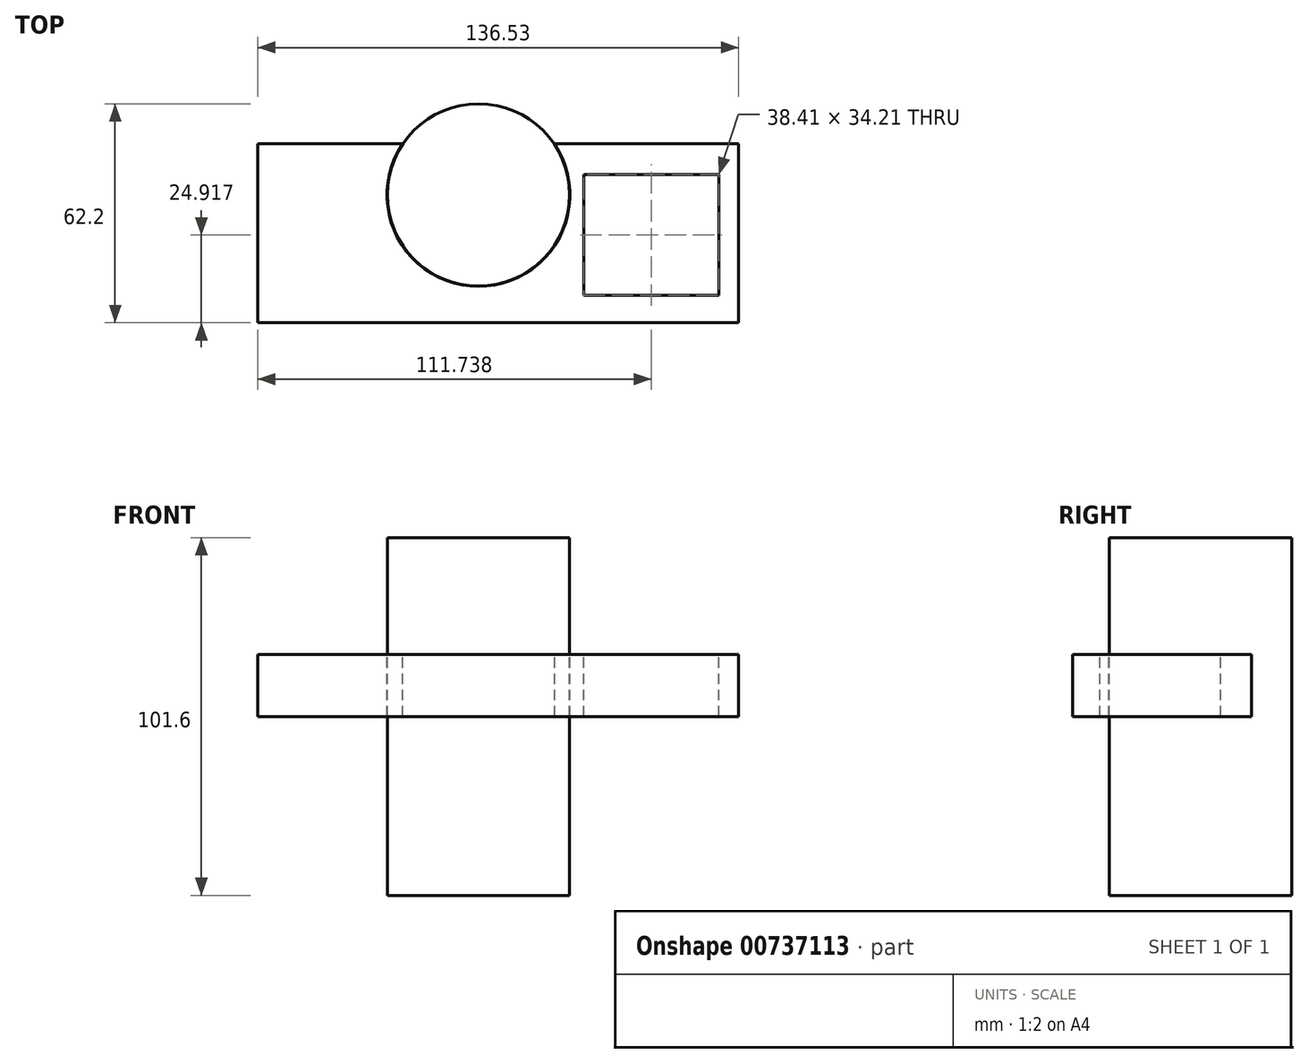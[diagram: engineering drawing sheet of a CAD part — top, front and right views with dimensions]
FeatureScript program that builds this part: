
annotation { "Feature Type Name" : "Feature", "Feature Type Description" : "" }
export const myFeature = defineFeature(function(context is Context, id is Id, definition is map)
    precondition{}
    {
        {
            var Q0;
            Q0=qCreatedBy(makeId("Front.planeOp"),FACE);
            var sketch = newSketch(context, id + "F0", { "sketchPlane" : qUnion([Q0])});
            skLineSegment(sketch, "E0.bottom", {"start": v(-42.1, 0) * mm, "end": v(94.42, 0) * mm});
            skLineSegment(sketch, "E0.top", {"start": v(-42.1, -17.58) * mm, "end": v(94.42, -17.58) * mm});
            skLineSegment(sketch, "E0.left", {"start": v(-42.1, 0) * mm, "end": v(-42.1, -17.58) * mm});
            skLineSegment(sketch, "E0.right", {"start": v(94.42, 0) * mm, "end": v(94.42, -17.58) * mm});
            skSolve(sketch);
        }
        {
            var Q0;
            Q0=makeQuery(id+"F0.imprint","IMPRINT",FACE,{"disambiguationData":[TD([[makeQuery(id+"F0.imprint","IMPRINT",EDGE,{"derivedFrom":sQuery(id+"F0.wireOp",EDGE,"E0.bottom")}),-1.0]])]});
            extrude(context, id + "F1", {"entities" : qUnion([Q0]), "depth" : 25.4 * mm, "offsetDistance" : 25.4 * mm, "hasSecondDirection" : true, "secondDirectionOppositeDirection" : true, "secondDirectionDepth" : 25.4 * mm});
        }
        {
            var Q0;
            Q0=makeQuery(id+"F1.opExtrude","SWEPT_FACE",FACE,{"disambiguationData":[OSD([sQuery(id+"F0.wireOp",EDGE,"E0.bottom")])]});
            var sketch = newSketch(context, id + "F2", { "sketchPlane" : qUnion([Q0])});
            skCircle(sketch, "E1", {"center": v(20.56, 10.92) * mm, "radius": 26 * mm});
            skSolve(sketch);
        }
        {
            var Q0;
            {var subQ0=sQuery(id+"F2.wireOp",EDGE,"E1");var subQ1=makeQuery(id+"F1.opExtrude","CAP_EDGE",EDGE,{"disambiguationData":[OSD([sQuery(id+"F0.wireOp",EDGE,"E0.bottom")])],"isStart":true});var subQ2=makeQuery(id+"F2.imprint","INTERSECT",VERTEX,{"disambiguationData":[OD(0.0)],"derivedFrom":[subQ1,subQ0]});Q0=makeQuery(id+"F2.imprint","IMPRINT",FACE,{"disambiguationData":[TD([[makeQuery(id+"F2.imprint","IMPRINT",EDGE,{"disambiguationData":[TD([[subQ2,1.0]])],"derivedFrom":subQ0}),1.0]])]});}
            var Q1;
            {var subQ0=sQuery(id+"F2.wireOp",EDGE,"E1");var subQ1=makeQuery(id+"F1.opExtrude","CAP_EDGE",EDGE,{"disambiguationData":[OSD([sQuery(id+"F0.wireOp",EDGE,"E0.bottom")])],"isStart":true});var subQ2=makeQuery(id+"F2.imprint","INTERSECT",VERTEX,{"disambiguationData":[OD(0.0)],"derivedFrom":[subQ1,subQ0]});Q1=makeQuery(id+"F2.imprint","IMPRINT",FACE,{"disambiguationData":[TD([[makeQuery(id+"F2.imprint","IMPRINT",EDGE,{"disambiguationData":[TD([[subQ2,-1.0]])],"derivedFrom":subQ0}),1.0]])]});}
            extrude(context, id + "F3", {"entities" : qUnion([Q0, Q1]), "operationType" : NewBodyOperationType.REMOVE, "oppositeDirection" : true, "depth" : 25.4 * mm, "offsetDistance" : 25.4 * mm});
        }
        {
            var Q0;
            Q0=makeQuery(id+"F1.opExtrude","SWEPT_FACE",FACE,{"disambiguationData":[OSD([sQuery(id+"F0.wireOp",EDGE,"E0.bottom")])]});
            var sketch = newSketch(context, id + "F4", { "sketchPlane" : qUnion([Q0])});
            skLineSegment(sketch, "E2.bottom", {"start": v(50.42, 16.62) * mm, "end": v(88.83, 16.62) * mm});
            skLineSegment(sketch, "E2.top", {"start": v(50.42, -17.59) * mm, "end": v(88.83, -17.59) * mm});
            skLineSegment(sketch, "E2.left", {"start": v(50.42, 16.62) * mm, "end": v(50.42, -17.59) * mm});
            skLineSegment(sketch, "E2.right", {"start": v(88.83, 16.62) * mm, "end": v(88.83, -17.59) * mm});
            skSolve(sketch);
        }
        {
            var Q0;
            Q0=makeQuery(id+"F4.imprint","IMPRINT",FACE,{"disambiguationData":[TD([[makeQuery(id+"F4.imprint","IMPRINT",EDGE,{"derivedFrom":sQuery(id+"F4.wireOp",EDGE,"E2.bottom")}),-1.0]])]});
            extrude(context, id + "F5", {"entities" : qUnion([Q0]), "operationType" : NewBodyOperationType.REMOVE, "oppositeDirection" : true, "depth" : 25.4 * mm, "offsetDistance" : 25.4 * mm});
        }
        {
            var Q0;
            Q0=makeQuery(id+"F1.opExtrude","SWEPT_FACE",FACE,{"disambiguationData":[OSD([sQuery(id+"F0.wireOp",EDGE,"E0.top")])]});
            var sketch = newSketch(context, id + "F6", { "sketchPlane" : qUnion([Q0])});
            skCircle(sketch, "E3", {"center": v(20.56, -10.92) * mm, "radius": 25.88 * mm});
            skSolve(sketch);
        }
        {
            var Q0;
            Q0=makeQuery(id+"F6.imprint","IMPRINT",FACE,{"disambiguationData":[TD([[makeQuery(id+"F6.imprint","IMPRINT",EDGE,{"derivedFrom":sQuery(id+"F6.wireOp",EDGE,"E3")}),1.0]])]});
            extrude(context, id + "F7", {"entities" : qUnion([Q0]), "depth" : 50.8 * mm, "offsetDistance" : 25.4 * mm, "hasSecondDirection" : true, "secondDirectionOppositeDirection" : true, "secondDirectionDepth" : 50.8 * mm});
        }
    });
